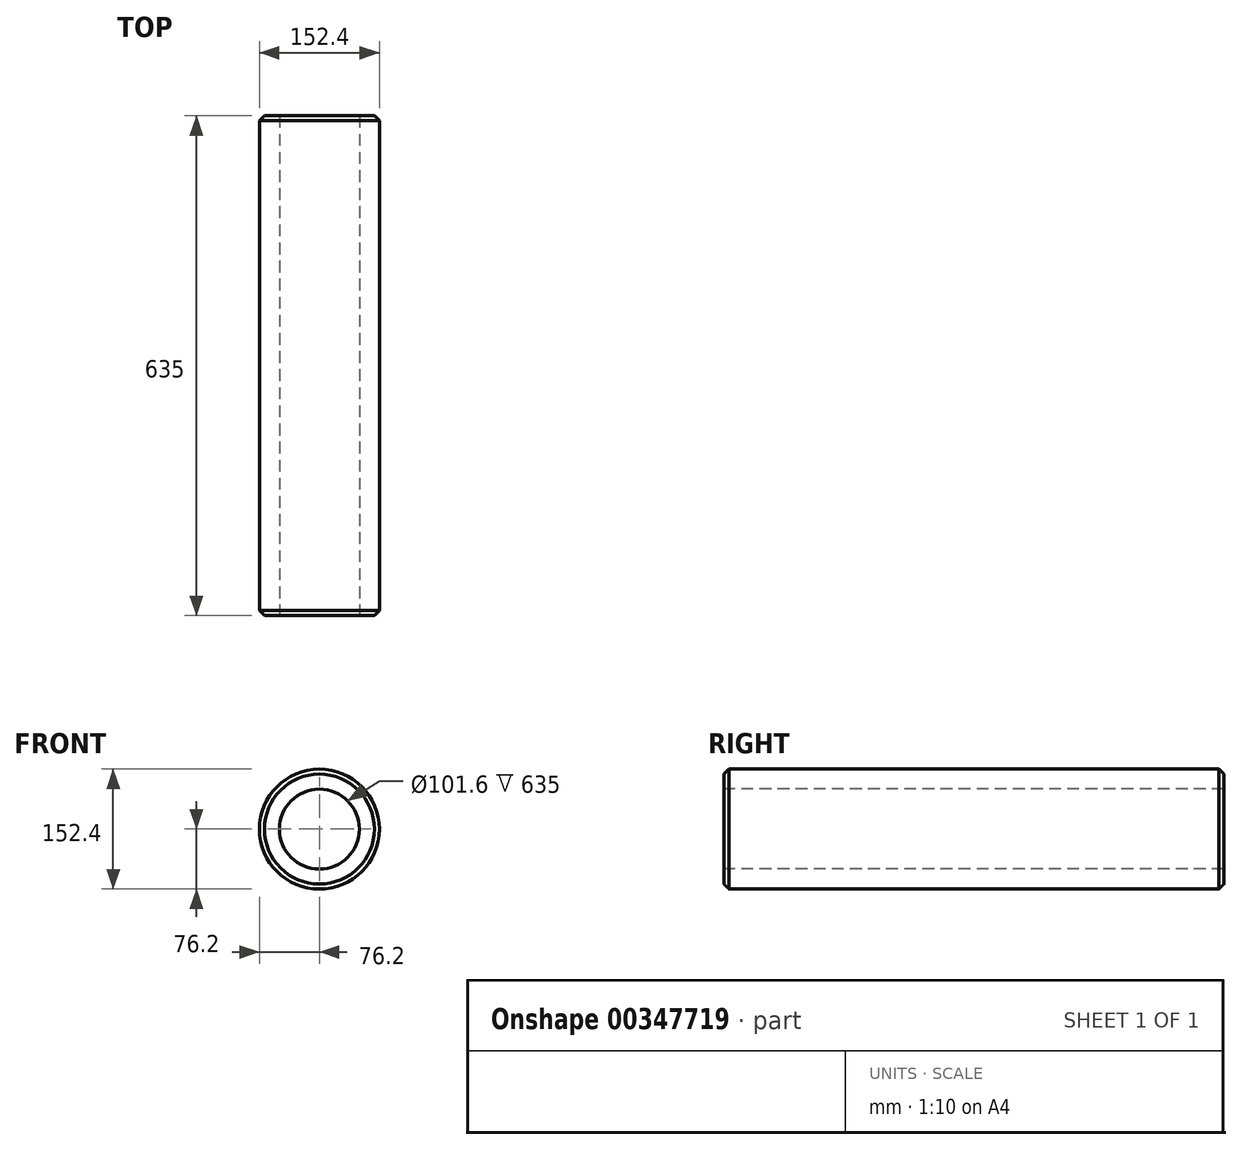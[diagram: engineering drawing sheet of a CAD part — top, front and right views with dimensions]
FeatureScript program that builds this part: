
annotation { "Feature Type Name" : "Feature", "Feature Type Description" : "" }
export const myFeature = defineFeature(function(context is Context, id is Id, definition is map)
    precondition{}
    {
        {
            var Q0;
            Q0=qCreatedBy(makeId("Front.planeOp"),FACE);
            var sketch = newSketch(context, id + "F0", { "sketchPlane" : qUnion([Q0])});
            skCircle(sketch, "E0", {"center": v(0, 0) * mm, "radius": 76.2 * mm});
            skSolve(sketch);
        }
        {
            var Q0;
            Q0 = qSketchRegion(id + "F0", true);
            extrude(context, id + "F1", {"entities" : qUnion([Q0]), "depth" : 635 * mm});
        }
        {
            var Q0;
            Q0=makeQuery(id+"F1.opExtrude","CAP_FACE",FACE,{"disambiguationData":[OSD([sQuery(id+"F0.wireOp",EDGE,"E0")])],"isStart":false});
            var sketch = newSketch(context, id + "F2", { "sketchPlane" : qUnion([Q0])});
            skCircle(sketch, "E1", {"center": v(0, 0) * mm, "radius": 50.8 * mm});
            skSolve(sketch);
        }
        {
            var Q0;
            Q0=sQuery(id+"F2.wireOp",VERTEX,"E1.center");
            var Q1;
            Q1=makeQuery(id+"F1.opExtrude","SWEPT_BODY",BODY,{"disambiguationData":[OSD([sQuery(id+"F0.wireOp",EDGE,"E0")])]});
            hole(context, id + "F3", {"style" : HoleStyle.SIMPLE, "endStyle" : HoleEndStyle.THROUGH, "holeDiameter" : 101.6 * mm, "isTappedThrough" : true, "tappedDepth" : 12.7 * mm, "tapClearance" : 3, "locations" : qUnion([Q0]), "scope" : qUnion([Q1])});
        }
        {
            var Q0;
            Q0=makeQuery(id+"F1.opExtrude","CAP_EDGE",EDGE,{"disambiguationData":[OSD([sQuery(id+"F0.wireOp",EDGE,"E0")])],"isStart":false});
            chamfer(context, id + "F4", {"entities" : qUnion([Q0]), "width" : 6.35 * mm, "tangentPropagation" : true});
        }
        {
            var Q0;
            Q0=makeQuery(id+"F1.opExtrude","CAP_EDGE",EDGE,{"disambiguationData":[OSD([sQuery(id+"F0.wireOp",EDGE,"E0")])],"isStart":true});
            chamfer(context, id + "F5", {"entities" : qUnion([Q0]), "width" : 6.35 * mm, "tangentPropagation" : true});
        }
    });
